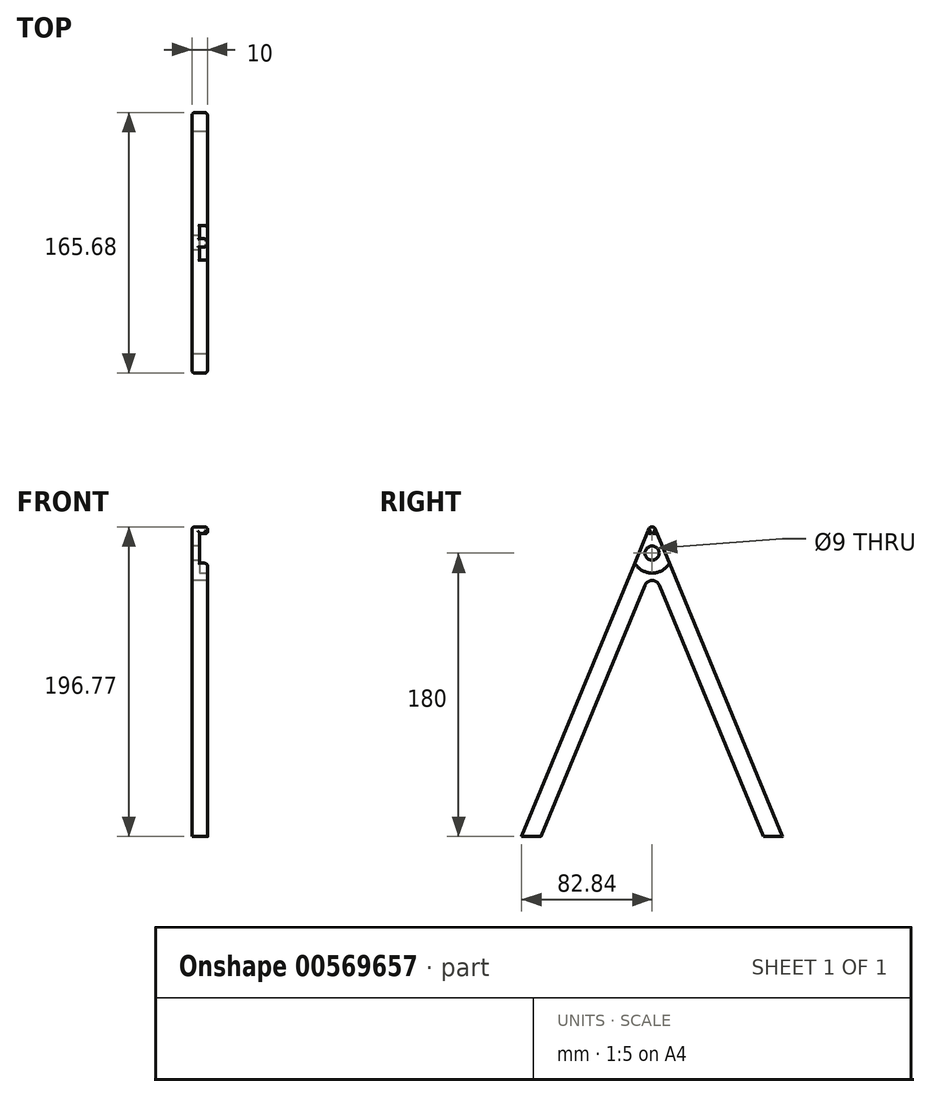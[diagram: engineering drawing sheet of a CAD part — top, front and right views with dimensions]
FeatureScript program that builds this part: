
annotation { "Feature Type Name" : "Feature", "Feature Type Description" : "" }
export const myFeature = defineFeature(function(context is Context, id is Id, definition is map)
    precondition{}
    {
        {
            var Q0;
            Q0=qCreatedBy(makeId("Right.planeOp"),FACE);
            var sketch = newSketch(context, id + "F0", { "sketchPlane" : qUnion([Q0])});
            skCircle(sketch, "E0", {"center": v(0, 0) * mm, "radius": 4.5 * mm});
            skLineSegment(sketch, "E1", {"start": v(0, 20) * mm, "end": v(-82.84, -180) * mm});
            skLineSegment(sketch, "E2", {"start": v(-82.84, -180) * mm, "end": v(82.84, -180) * mm});
            skLineSegment(sketch, "E3", {"start": v(82.84, -180) * mm, "end": v(0, 20) * mm});
            skLineSegment(sketch, "E4", {"start": v(-70.71, -180) * mm, "end": v(0, -9.28) * mm});
            skLineSegment(sketch, "E5.MirrorCS", {"start": v(70.71, -180) * mm, "end": v(0, -9.28) * mm});
            skSolve(sketch);
        }
        {
            var Q0;
            Q0=makeQuery(id+"F0.imprint","IMPRINT",FACE,{"disambiguationData":[TD([[makeQuery(id+"F0.imprint","IMPRINT",EDGE,{"derivedFrom":sQuery(id+"F0.wireOp",EDGE,"E0")}),-1.0]])]});
            extrude(context, id + "F1", {"entities" : qUnion([Q0]), "depth" : 10 * mm, "offsetDistance" : 25 * mm});
        }
        {
            var Q0;
            Q0=makeQuery(id+"F1.opExtrude","SWEPT_EDGE",EDGE,{"disambiguationData":[OSD([sQuery(id+"F0.wireOp",EDGE,"E1"),sQuery(id+"F0.wireOp",EDGE,"E3")])]});
            var Q1;
            Q1=makeQuery(id+"F1.opExtrude","CAP_EDGE",EDGE,{"disambiguationData":[OSD([sQuery(id+"F0.wireOp",EDGE,"E1")])],"isStart":false});
            var Q2;
            Q2=makeQuery(id+"F1.opExtrude","CAP_EDGE",EDGE,{"disambiguationData":[OSD([sQuery(id+"F0.wireOp",EDGE,"E1")])],"isStart":true});
            var Q3;
            Q3=makeQuery(id+"F1.opExtrude","CAP_EDGE",EDGE,{"disambiguationData":[OSD([sQuery(id+"F0.wireOp",EDGE,"E3")])],"isStart":true});
            var Q4;
            Q4=makeQuery(id+"F1.opExtrude","CAP_EDGE",EDGE,{"disambiguationData":[OSD([sQuery(id+"F0.wireOp",EDGE,"E3")])],"isStart":false});
            fillet(context, id + "F2", {"entities" : qUnion([Q0, Q1, Q2, Q3, Q4]), "radius" : 2 * mm, "tangentPropagation" : true, "allowEdgeOverflow" : false});
        }
        {
            var Q0;
            Q0=makeQuery(id+"F1.opExtrude","SWEPT_EDGE",EDGE,{"disambiguationData":[OSD([sQuery(id+"F0.wireOp",EDGE,"E4"),sQuery(id+"F0.wireOp",EDGE,"E5.MirrorCS")])]});
            fillet(context, id + "F3", {"entities" : qUnion([Q0]), "radius" : 5 * mm, "tangentPropagation" : true, "allowEdgeOverflow" : false});
        }
        {
            var Q0;
            Q0=makeQuery(id+"F1.opExtrude","CAP_FACE",FACE,{"disambiguationData":[OSD([sQuery(id+"F0.wireOp",EDGE,"E0"),sQuery(id+"F0.wireOp",EDGE,"E1"),sQuery(id+"F0.wireOp",EDGE,"E2"),sQuery(id+"F0.wireOp",EDGE,"E3"),sQuery(id+"F0.wireOp",EDGE,"E4"),sQuery(id+"F0.wireOp",EDGE,"E5.MirrorCS")])],"isStart":false});
            var sketch = newSketch(context, id + "F4", { "sketchPlane" : qUnion([Q0])});
            skCircle(sketch, "E6", {"center": v(0, 0) * mm, "radius": 12.65 * mm});
            skSolve(sketch);
        }
        {
            var Q0;
            {var subQ0=sQuery(id+"F4.wireOp",EDGE,"E6");var subQ1=sQuery(id+"F0.wireOp",EDGE,"E1");var subQ2=makeQuery(id+"F2.opFillet","BLEND_EDGE",EDGE,{"blendedFrom":[makeQuery(id+"F1.opExtrude","CAP_EDGE",EDGE,{"disambiguationData":[OSD([subQ1])],"isStart":false}),makeQuery(id+"F1.opExtrude","CAP_FACE",FACE,{"disambiguationData":[OSD([sQuery(id+"F0.wireOp",EDGE,"E0"),subQ1,sQuery(id+"F0.wireOp",EDGE,"E2"),sQuery(id+"F0.wireOp",EDGE,"E3"),sQuery(id+"F0.wireOp",EDGE,"E4"),sQuery(id+"F0.wireOp",EDGE,"E5.MirrorCS")])],"isStart":false})],"blendedInto":[makeQuery(id+"F1.opExtrude","CAP_FACE",FACE,{"disambiguationData":[OSD([sQuery(id+"F0.wireOp",EDGE,"E0"),subQ1,sQuery(id+"F0.wireOp",EDGE,"E2"),sQuery(id+"F0.wireOp",EDGE,"E3"),sQuery(id+"F0.wireOp",EDGE,"E4"),sQuery(id+"F0.wireOp",EDGE,"E5.MirrorCS")])],"isStart":false})]});var subQ3=makeQuery(id+"F4.imprint","INTERSECT",VERTEX,{"disambiguationData":[OD(0.0)],"derivedFrom":[subQ2,subQ0]});Q0=makeQuery(id+"F4.imprint","IMPRINT",FACE,{"disambiguationData":[TD([[makeQuery(id+"F4.imprint","IMPRINT",EDGE,{"disambiguationData":[TD([[subQ3,-1.0]])],"derivedFrom":subQ0}),1.0]])]});}
            var Q1;
            {var subQ0=sQuery(id+"F4.wireOp",EDGE,"E6");var subQ1=sQuery(id+"F0.wireOp",EDGE,"E3");var subQ2=makeQuery(id+"F2.opFillet","BLEND_EDGE",EDGE,{"blendedFrom":[makeQuery(id+"F1.opExtrude","CAP_EDGE",EDGE,{"disambiguationData":[OSD([subQ1])],"isStart":false}),makeQuery(id+"F1.opExtrude","CAP_FACE",FACE,{"disambiguationData":[OSD([sQuery(id+"F0.wireOp",EDGE,"E0"),sQuery(id+"F0.wireOp",EDGE,"E1"),sQuery(id+"F0.wireOp",EDGE,"E2"),subQ1,sQuery(id+"F0.wireOp",EDGE,"E4"),sQuery(id+"F0.wireOp",EDGE,"E5.MirrorCS")])],"isStart":false})],"blendedInto":[makeQuery(id+"F1.opExtrude","CAP_FACE",FACE,{"disambiguationData":[OSD([sQuery(id+"F0.wireOp",EDGE,"E0"),sQuery(id+"F0.wireOp",EDGE,"E1"),sQuery(id+"F0.wireOp",EDGE,"E2"),subQ1,sQuery(id+"F0.wireOp",EDGE,"E4"),sQuery(id+"F0.wireOp",EDGE,"E5.MirrorCS")])],"isStart":false})]});var subQ3=makeQuery(id+"F4.imprint","INTERSECT",VERTEX,{"disambiguationData":[OD(0.0)],"derivedFrom":[subQ2,subQ0]});Q1=makeQuery(id+"F4.imprint","IMPRINT",FACE,{"disambiguationData":[TD([[makeQuery(id+"F4.imprint","IMPRINT",EDGE,{"disambiguationData":[TD([[subQ3,1.0]])],"derivedFrom":subQ0}),1.0]])]});}
            var Q2;
            {var subQ0=sQuery(id+"F0.wireOp",EDGE,"E0");Q2=makeQuery(id+"F4.imprint","IMPRINT",FACE,{"disambiguationData":[TD([[makeQuery(id+"F4.imprint","IMPRINT",EDGE,{"derivedFrom":makeQuery(id+"F1.opExtrude","CAP_EDGE",EDGE,{"disambiguationData":[OSD([subQ0])],"isStart":false})}),-1.0]])]});}
            extrude(context, id + "F5", {"entities" : qUnion([Q0, Q1, Q2]), "operationType" : NewBodyOperationType.REMOVE, "oppositeDirection" : true, "depth" : 5 * mm, "offsetDistance" : 25 * mm});
        }
        {
            var Q0;
            Q0=makeQuery(id+"F5.boolean.opBoolean","COPY",EDGE,{"disambiguationData":[OD(0.0)],"derivedFrom":makeQuery(id+"F5.opExtrude","CAP_EDGE",EDGE,{"disambiguationData":[OSD([sQuery(id+"F4.wireOp",EDGE,"E6")])],"isStart":true})});
            var Q1;
            Q1=makeQuery(id+"F5.boolean.opBoolean","COPY",EDGE,{"disambiguationData":[OD(1.0)],"derivedFrom":makeQuery(id+"F5.opExtrude","CAP_EDGE",EDGE,{"disambiguationData":[OSD([sQuery(id+"F4.wireOp",EDGE,"E6")])],"isStart":true})});
            var Q2;
            Q2=makeQuery(id+"F5.boolean.opBoolean","INTERSECT",EDGE,{"derivedFrom":[makeQuery(id+"F1.opExtrude","SWEPT_FACE",FACE,{"disambiguationData":[OSD([sQuery(id+"F0.wireOp",EDGE,"E1")])]}),makeQuery(id+"F5.opExtrude","CAP_FACE",FACE,{"disambiguationData":[OSD([sQuery(id+"F0.wireOp",EDGE,"E0"),sQuery(id+"F4.wireOp",EDGE,"E6")])],"isStart":false})]});
            var Q3;
            Q3=makeQuery(id+"F5.boolean.opBoolean","INTERSECT",EDGE,{"derivedFrom":[makeQuery(id+"F1.opExtrude","SWEPT_FACE",FACE,{"disambiguationData":[OSD([sQuery(id+"F0.wireOp",EDGE,"E3")])]}),makeQuery(id+"F5.opExtrude","CAP_FACE",FACE,{"disambiguationData":[OSD([sQuery(id+"F0.wireOp",EDGE,"E0"),sQuery(id+"F4.wireOp",EDGE,"E6")])],"isStart":false})]});
            fillet(context, id + "F6", {"entities" : qUnion([Q0, Q1, Q2, Q3]), "radius" : 1 * mm, "tangentPropagation" : true, "allowEdgeOverflow" : false});
        }
        {
            var Q0;
            Q0=makeQuery(id+"F1.opExtrude","CAP_EDGE",EDGE,{"disambiguationData":[OSD([sQuery(id+"F0.wireOp",EDGE,"E4")])],"isStart":false});
            var Q1;
            Q1=makeQuery(id+"F1.opExtrude","CAP_EDGE",EDGE,{"disambiguationData":[OSD([sQuery(id+"F0.wireOp",EDGE,"E5.MirrorCS")])],"isStart":false});
            var Q2;
            Q2=makeQuery(id+"F1.opExtrude","CAP_EDGE",EDGE,{"disambiguationData":[OSD([sQuery(id+"F0.wireOp",EDGE,"E5.MirrorCS")])],"isStart":true});
            var Q3;
            Q3=makeQuery(id+"F1.opExtrude","CAP_EDGE",EDGE,{"disambiguationData":[OSD([sQuery(id+"F0.wireOp",EDGE,"E4")])],"isStart":true});
            var Q4;
            {var subQ0=sQuery(id+"F0.wireOp",EDGE,"E5.MirrorCS");var subQ1=sQuery(id+"F0.wireOp",EDGE,"E4");Q4=makeQuery(id+"F3.opFillet","BLEND_EDGE",EDGE,{"blendedFrom":[makeQuery(id+"F1.opExtrude","SWEPT_EDGE",EDGE,{"disambiguationData":[OSD([subQ1,subQ0])]}),makeQuery(id+"F1.opExtrude","CAP_FACE",FACE,{"disambiguationData":[OSD([sQuery(id+"F0.wireOp",EDGE,"E0"),sQuery(id+"F0.wireOp",EDGE,"E1"),sQuery(id+"F0.wireOp",EDGE,"E2"),sQuery(id+"F0.wireOp",EDGE,"E3"),subQ1,subQ0])],"isStart":true})],"blendedInto":[makeQuery(id+"F1.opExtrude","CAP_FACE",FACE,{"disambiguationData":[OSD([sQuery(id+"F0.wireOp",EDGE,"E0"),sQuery(id+"F0.wireOp",EDGE,"E1"),sQuery(id+"F0.wireOp",EDGE,"E2"),sQuery(id+"F0.wireOp",EDGE,"E3"),subQ1,subQ0])],"isStart":true})]});}
            fillet(context, id + "F7", {"entities" : qUnion([Q0, Q1, Q2, Q3, Q4]), "radius" : 1 * mm, "tangentPropagation" : true, "allowEdgeOverflow" : false});
        }
    });
